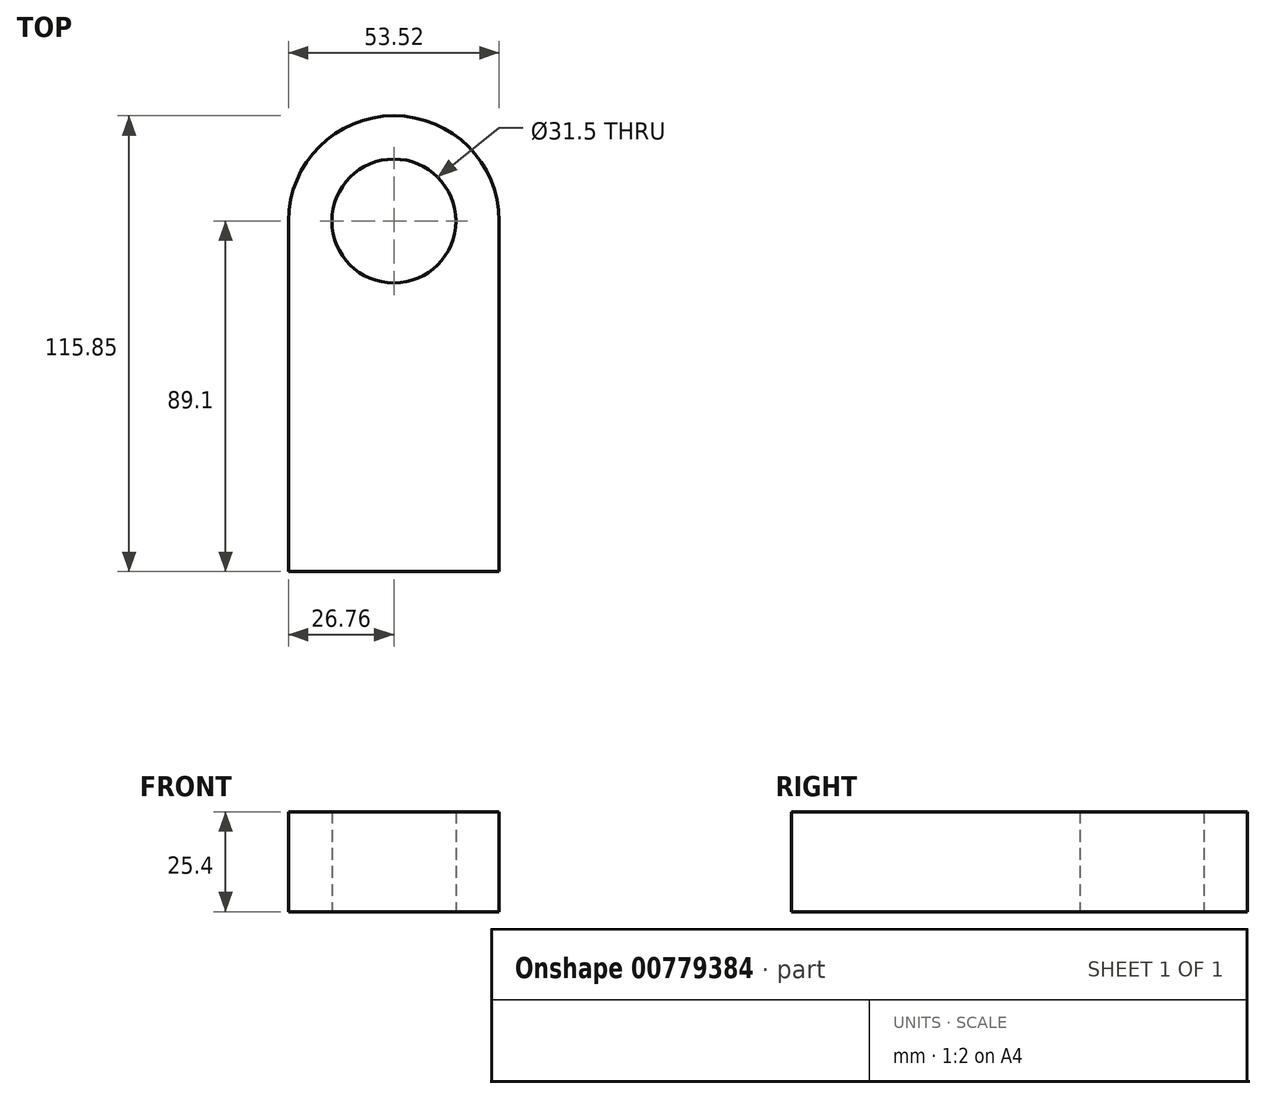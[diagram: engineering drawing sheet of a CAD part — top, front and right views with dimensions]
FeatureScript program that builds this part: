
annotation { "Feature Type Name" : "Feature", "Feature Type Description" : "" }
export const myFeature = defineFeature(function(context is Context, id is Id, definition is map)
    precondition{}
    {
        {
            var Q0;
            Q0=qCreatedBy(makeId("Top.planeOp"),FACE);
            var sketch = newSketch(context, id + "F0", { "sketchPlane" : qUnion([Q0])});
            skLineSegment(sketch, "E0.top", {"start": v(-26.76, -44.55) * mm, "end": v(26.76, -44.55) * mm});
            skLineSegment(sketch, "E0.left", {"start": v(-26.76, 44.55) * mm, "end": v(-26.76, -44.55) * mm});
            skLineSegment(sketch, "E0.right", {"start": v(26.76, 44.55) * mm, "end": v(26.76, -44.55) * mm});
            skPoint(sketch, "E0.middle", {"position": v(0, 0) * mm});
            skArc(sketch, "E1", {"start": v(26.76, 44.55) * mm, "mid": v(0, 71.3) * mm, "end": v(-26.76, 44.55) * mm});
            skCircle(sketch, "E2", {"center": v(0, 44.55) * mm, "radius": 15.75 * mm});
            skSolve(sketch);
        }
        {
            var Q0;
            Q0=makeQuery(id+"F0.imprint","IMPRINT",FACE,{"disambiguationData":[TD([[makeQuery(id+"F0.imprint","IMPRINT",EDGE,{"derivedFrom":sQuery(id+"F0.wireOp",EDGE,"E0.top")}),1.0]])]});
            extrude(context, id + "F1", {"entities" : qUnion([Q0]), "depth" : 25.4 * mm, "offsetDistance" : 25.4 * mm});
        }
    });
